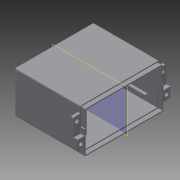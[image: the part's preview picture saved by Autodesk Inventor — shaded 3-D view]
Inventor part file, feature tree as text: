
AUTODESK INVENTOR PART (.ipt)
format: ipt  version: 2015 (Build 190159000, 159)  size: 274,432 bytes
history: native  units: in
note: dims shown in document units (in); Inventor stores cm internally (conversion verified against a paired STEP export)
features: extrude x11, sketch x11, fillet x4, mirror x2, plane x1
ambient origin geometry x8: Origin, YZ Plane, XZ Plane, XY Plane, X Axis, Y Axis, Z Axis, Center Point
bodies: Solid1 (feature_tree)
feature tree (29):
  extrude  "Extrusion1"  Depth=1.9094in
  extrude  "Extrusion2"  Depth=2.2835in
  extrude  "Extrusion3"  Depth=0.0591in
  fillet  "Fillet1"  Radius=0.0591in
  extrude  "Extrusion4"  Depth=1.1024in TaperAngle=0.0deg
  plane  "Work Plane1"
  extrude  "Extrusion5"  Depth=0.0394in
  mirror  "Mirror1"
  extrude  "Extrusion6"  Depth=0.3937in
  fillet  "Fillet2"  Radius=0.5906in
  extrude  "Extrusion7"  Depth=0.0394in
  fillet  "Fillet3"  Radius=0.0394in
  extrude  "Extrusion8"  Depth=0.5906in
  extrude  "Extrusion9"  Depth=0.0787in TaperAngle=0.0deg
  fillet  "Fillet4"  Radius=0.0394in
  extrude  "Extrusion10"  Depth=0.3937in
  extrude  "Extrusion11"  Depth=0.0787in TaperAngle=0.0deg
  mirror  "Mirror2"
  sketch  "Sketch1"  dims[d0=2.1654in d1=1.9094in]
  sketch  "Sketch2"  dims[d2=2.0276in d3=2.2835in]
  sketch  "Sketch3"  dims[d4=0.0591in d5=0.0591in d6=0.0591in d7=0.0in]
  sketch  "Sketch4"  dims[d8=2.1654in d9=1.1024in d10=0.0in]
  sketch  "Sketch5"  dims[d11=0.0591in d12=0.0in d13=0.0394in]
  sketch  "Sketch6"  dims[d14=0.1299in d15=0.3937in d16=0.5906in]
  sketch  "Sketch7"  dims[d17=0.3937in d18=0.0in d19=1.0827in d20=0.0394in]
  sketch  "Sketch8"  dims[d21=0.1772in d22=0.5906in]
  sketch  "Sketch9"  dims[d23=0.3937in d24=0.0787in d25=0.0in d26=0.0394in]
  sketch  "Sketch10"  dims[d27=0.8661in d28=0.3937in]
  sketch  "Sketch11"  dims[d29=0.5118in d30=0.0787in d31=0.0in d32=0.0197in d33=0.0295in d34=0.0295in d35=0.0in d36=0.0295in d37=0.0in d38=0.0295in d39=0.0295in d40=0.502in d41=0.0in d42=0.1181in d43=0.0in d44=0.0394in d45=2.2835in d46=0.4921in d47=0.0295in d48=0.0in d49=0.0295in d50=0.0295in d51=0.1181in d52=0.0in d60=0.0787in d61=0.502in d62=0.1969in d63=0.1969in d64=0.2854in d65=0.0in d66=0.1969in d67=0.0in d68=0.0394in d69=0.1181in d70=0.0984in d71=0.1378in d72=0.0787in d73=0.0in d74=0.1181in d75=0.1378in d76=0.0984in d77=0.1969in d78=0.0in]
